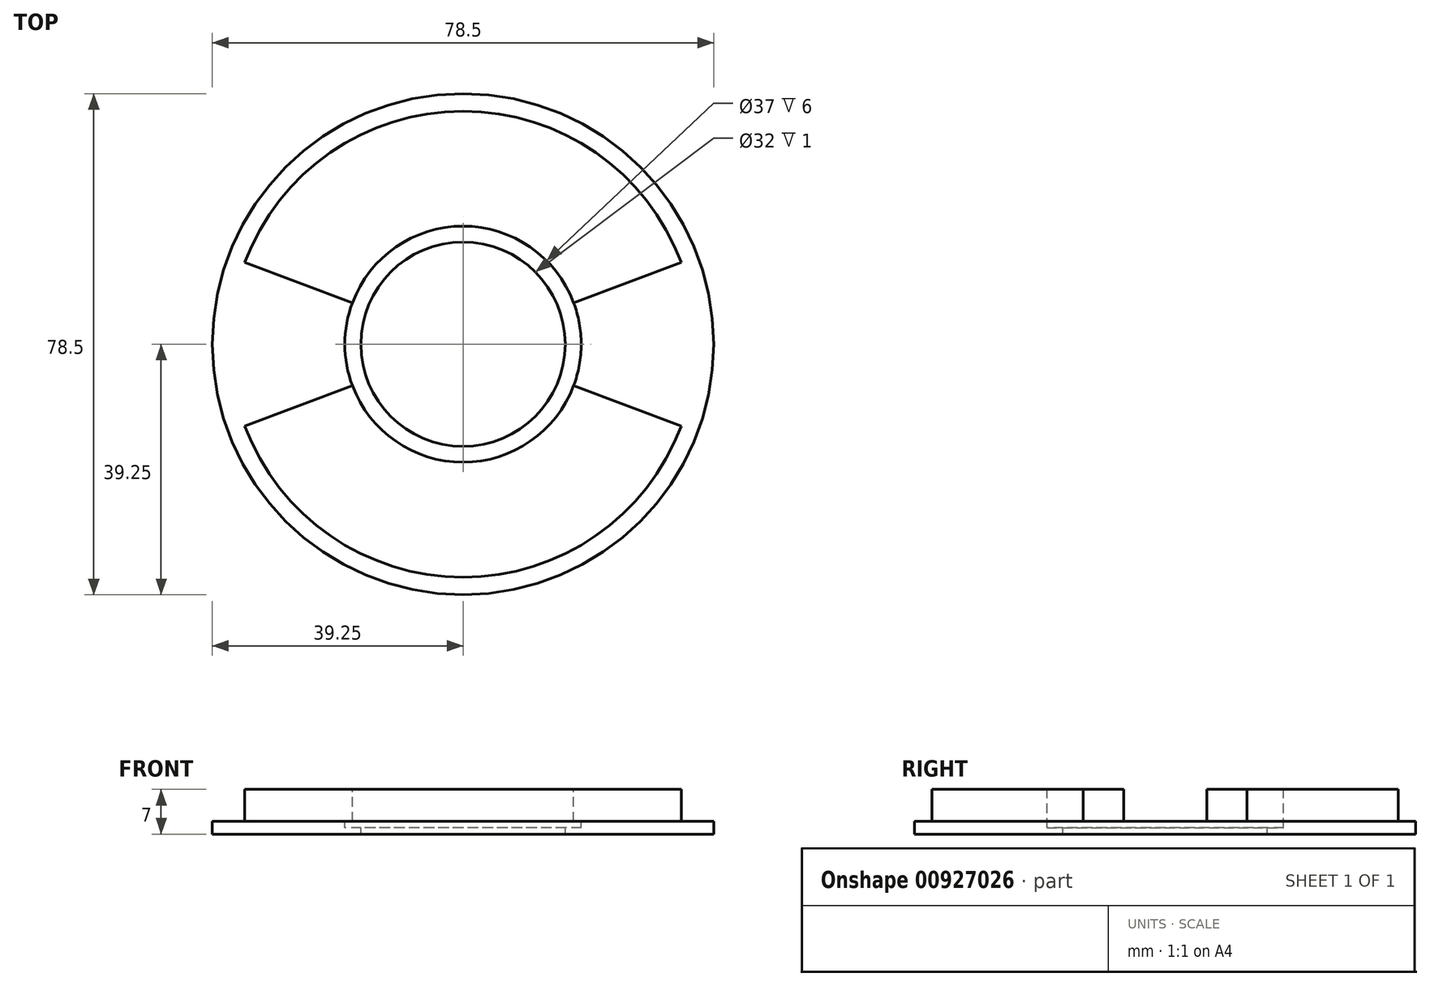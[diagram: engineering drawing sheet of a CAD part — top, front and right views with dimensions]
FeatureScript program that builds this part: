
annotation { "Feature Type Name" : "Feature", "Feature Type Description" : "" }
export const myFeature = defineFeature(function(context is Context, id is Id, definition is map)
    precondition{}
    {
        {
            var Q0;
            Q0=qCreatedBy(makeId("Top.planeOp"),FACE);
            var sketch = newSketch(context, id + "F0", { "sketchPlane" : qUnion([Q0])});
            skCircle(sketch, "E0", {"center": v(0, 0) * mm, "radius": 39.25 * mm});
            skCircle(sketch, "E1", {"center": v(0, 0) * mm, "radius": 36.5 * mm});
            skCircle(sketch, "E2", {"center": v(0, 0) * mm, "radius": 31.5 * mm});
            skSolve(sketch);
        }
        {
            var Q0;
            Q0=makeQuery(id+"F0.imprint","IMPRINT",FACE,{"disambiguationData":[TD([[makeQuery(id+"F0.imprint","IMPRINT",EDGE,{"derivedFrom":sQuery(id+"F0.wireOp",EDGE,"E2")}),1.0]])]});
            var Q1;
            Q1=makeQuery(id+"F0.imprint","IMPRINT",FACE,{"disambiguationData":[TD([[makeQuery(id+"F0.imprint","IMPRINT",EDGE,{"derivedFrom":sQuery(id+"F0.wireOp",EDGE,"E1")}),1.0]])]});
            extrude(context, id + "F1", {"entities" : qUnion([Q0, Q1]), "depth" : 7 * mm, "offsetDistance" : 25 * mm});
        }
        {
            var Q0;
            Q0=makeQuery(id+"F0.imprint","IMPRINT",FACE,{"disambiguationData":[TD([[makeQuery(id+"F0.imprint","IMPRINT",EDGE,{"derivedFrom":sQuery(id+"F0.wireOp",EDGE,"E0")}),1.0]])]});
            var Q1;
            Q1=makeQuery(id+"F0.imprint","IMPRINT",FACE,{"disambiguationData":[TD([[makeQuery(id+"F0.imprint","IMPRINT",EDGE,{"derivedFrom":sQuery(id+"F0.wireOp",EDGE,"E1")}),1.0]])]});
            extrude(context, id + "F2", {"entities" : qUnion([Q0, Q1]), "operationType" : NewBodyOperationType.ADD, "depth" : 2 * mm, "offsetDistance" : 25 * mm});
        }
        {
            var Q0;
            Q0=makeQuery(id+"F1.opExtrude","CAP_FACE",FACE,{"disambiguationData":[OSD([sQuery(id+"F0.wireOp",EDGE,"E1")])],"isStart":false});
            var sketch = newSketch(context, id + "F3", { "sketchPlane" : qUnion([Q0])});
            skCircle(sketch, "E3", {"center": v(0, 0) * mm, "radius": 18.5 * mm});
            skCircle(sketch, "E4", {"center": v(0, 0) * mm, "radius": 16 * mm});
            skSolve(sketch);
        }
        {
            var Q0;
            Q0=qSketchRegion(id+"F3",true);
            var Q1;
            Q1=makeQuery(id+"F3.imprint","IMPRINT",FACE,{"disambiguationData":[TD([[makeQuery(id+"F3.imprint","IMPRINT",EDGE,{"derivedFrom":sQuery(id+"F3.wireOp",EDGE,"E4")}),1.0]])]});
            extrude(context, id + "F4", {"entities" : qUnion([Q0, Q1]), "operationType" : NewBodyOperationType.REMOVE, "oppositeDirection" : true, "depth" : 6 * mm, "offsetDistance" : 25 * mm});
        }
        {
            var Q0;
            Q0=makeQuery(id+"F3.imprint","IMPRINT",FACE,{"disambiguationData":[TD([[makeQuery(id+"F3.imprint","IMPRINT",EDGE,{"derivedFrom":sQuery(id+"F3.wireOp",EDGE,"E4")}),1.0]])]});
            extrude(context, id + "F5", {"entities" : qUnion([Q0]), "operationType" : NewBodyOperationType.REMOVE, "oppositeDirection" : true, "depth" : 25 * mm, "offsetDistance" : 25 * mm});
        }
        {
            var Q0;
            Q0=makeQuery(id+"F1.opExtrude","CAP_FACE",FACE,{"disambiguationData":[OSD([sQuery(id+"F0.wireOp",EDGE,"E1")])],"isStart":false});
            var sketch = newSketch(context, id + "F6", { "sketchPlane" : qUnion([Q0])});
            skLineSegment(sketch, "E5.bottom", {"start": v(40, -6.5) * mm, "end": v(-40, -6.5) * mm});
            skLineSegment(sketch, "E5.top", {"start": v(40, 6.5) * mm, "end": v(-40, 6.5) * mm});
            skLineSegment(sketch, "E5.left", {"start": v(40, -6.5) * mm, "end": v(40, 6.5) * mm});
            skLineSegment(sketch, "E5.right", {"start": v(-40, -6.5) * mm, "end": v(-40, 6.5) * mm});
            skPoint(sketch, "E5.middle", {"position": v(0, 0) * mm});
            skLineSegment(sketch, "E6", {"start": v(-17.32, 6.5) * mm, "end": v(-34.17, 12.82) * mm});
            skLineSegment(sketch, "E7.MirrorCS", {"start": v(17.32, 6.5) * mm, "end": v(34.17, 12.82) * mm});
            skLineSegment(sketch, "E8.MirrorCS", {"start": v(-17.32, -6.5) * mm, "end": v(-34.17, -12.82) * mm});
            skLineSegment(sketch, "E9.MirrorCS", {"start": v(17.32, -6.5) * mm, "end": v(34.17, -12.82) * mm});
            skSolve(sketch);
        }
        {
            var Q0;
            Q0=qSketchRegion(id+"F6",true);
            var Q1;
            {var subQ0=sQuery(id+"F6.wireOp",EDGE,"E6");Q1=makeQuery(id+"F6.imprint","IMPRINT",FACE,{"disambiguationData":[TD([[makeQuery(id+"F6.imprint","IMPRINT",EDGE,{"derivedFrom":subQ0}),1.0]])]});}
            var Q2;
            {var subQ0=sQuery(id+"F6.wireOp",EDGE,"E8.MirrorCS");Q2=makeQuery(id+"F6.imprint","IMPRINT",FACE,{"disambiguationData":[TD([[makeQuery(id+"F6.imprint","IMPRINT",EDGE,{"derivedFrom":subQ0}),-1.0]])]});}
            var Q3;
            {var subQ0=sQuery(id+"F6.wireOp",EDGE,"E9.MirrorCS");Q3=makeQuery(id+"F6.imprint","IMPRINT",FACE,{"disambiguationData":[TD([[makeQuery(id+"F6.imprint","IMPRINT",EDGE,{"derivedFrom":subQ0}),1.0]])]});}
            var Q4;
            {var subQ0=sQuery(id+"F6.wireOp",EDGE,"E7.MirrorCS");Q4=makeQuery(id+"F6.imprint","IMPRINT",FACE,{"disambiguationData":[TD([[makeQuery(id+"F6.imprint","IMPRINT",EDGE,{"derivedFrom":subQ0}),-1.0]])]});}
            extrude(context, id + "F7", {"entities" : qUnion([Q0, Q1, Q2, Q3, Q4]), "operationType" : NewBodyOperationType.REMOVE, "oppositeDirection" : true, "depth" : 5 * mm, "offsetDistance" : 25 * mm});
        }
    });
